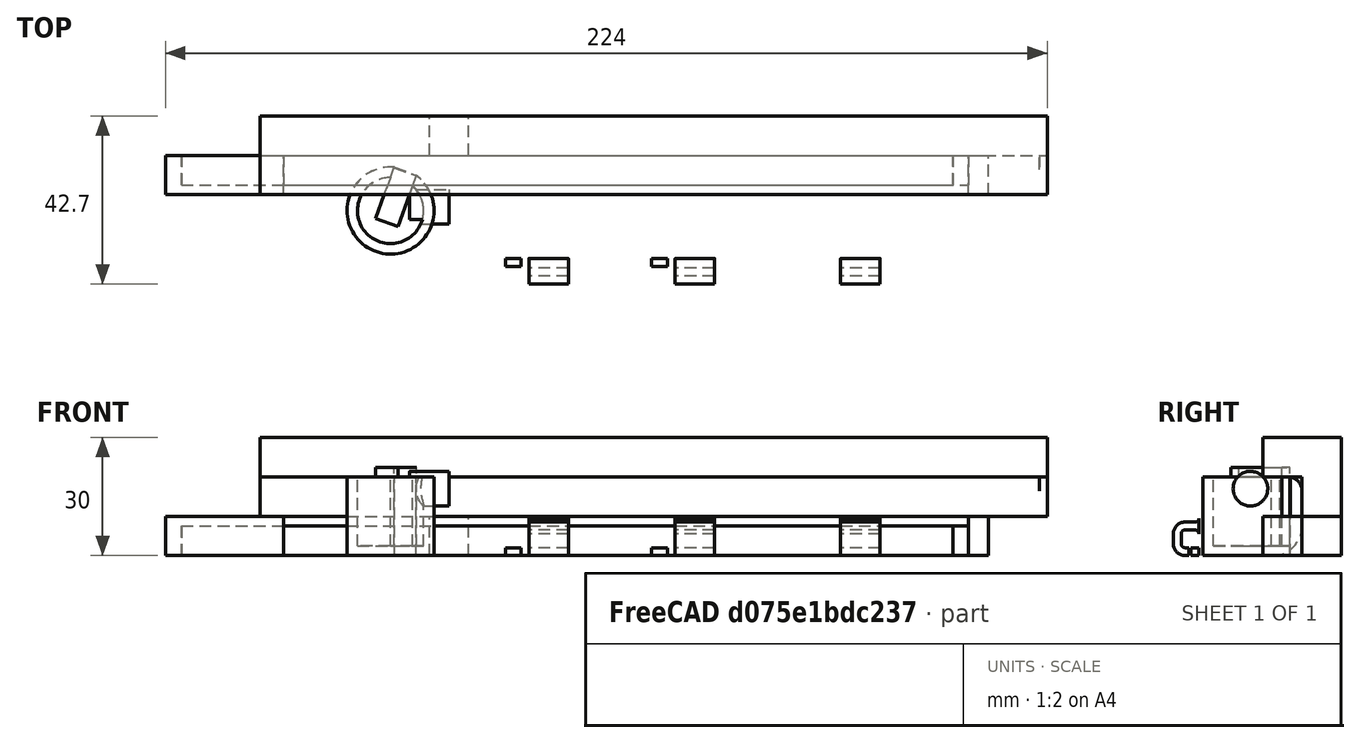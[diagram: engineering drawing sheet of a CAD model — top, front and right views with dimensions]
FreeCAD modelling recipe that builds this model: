
FCSTD DOCUMENT  (FreeCAD 0.19R0.19.2)
Label: v0_74
License: All rights reserved
LicenseURL: http://en.wikipedia.org/wiki/All_rights_reserved
objects: Part::Box×35, Part::Fillet×31, Part::MultiFuse×14, Part::Cut×13, Sketcher::SketchObject×11, Part::Extrusion×9, Part::Cylinder×6, App::MeasureDistance×5, Part::Revolution×1
note: 120 computed .brp shape members not serialized (recipe doc carries the construction recipe); baked Part::Feature solids carry a one-line shape summary decoded from their .brp

FEATURE [Sketcher::SketchObject] Sketch001
  FullyConstrained = true
  sketch-geometry (47):
    g0: Circle CenterX=-129.5 CenterY=-8 CenterZ=0 NormalX=0 NormalY=0 NormalZ=1 AngleXU=0 Radius=1
    g1: Circle CenterX=-129.5 CenterY=-3 CenterZ=0 NormalX=0 NormalY=0 NormalZ=1 AngleXU=0 Radius=1
    g2: Circle CenterX=-124.5 CenterY=-3 CenterZ=0 NormalX=0 NormalY=0 NormalZ=1 AngleXU=0 Radius=1
    g3: BSplineCurve PolesCount=3 KnotsCount=2 Degree=2 IsPeriodic=0
    g4: GeomPoint X=-129.5 Y=-8 Z=0
    g5: GeomPoint X=-124.5 Y=-3 Z=0
    g6: LineSegment StartX=18.6 StartY=-2.9 StartZ=0 EndX=23.6 EndY=-2.9 EndZ=0
    g7: ArcOfCircle CenterX=23.8 CenterY=-14.35 CenterZ=0 NormalX=0 NormalY=0 NormalZ=1 AngleXU=0 Radius=2.3 StartAngle=8e-16 EndAngle=1.5708
    g8: ArcOfCircle CenterX=23.8 CenterY=-18.1 CenterZ=0 NormalX=0 NormalY=0 NormalZ=1 AngleXU=0 Radius=2.3 StartAngle=4.71239 EndAngle=6.28319
    g9: LineSegment StartX=23.8 StartY=-20.4 StartZ=0 EndX=21.1 EndY=-20.4 EndZ=0
    g10: LineSegment StartX=21.1 StartY=-22.9 StartZ=0 EndX=21.1 EndY=-20.4 EndZ=0
    g11: LineSegment StartX=26.1 StartY=-14.35 StartZ=0 EndX=26.1 EndY=-18.1 EndZ=0
    g12: LineSegment StartX=18.6 StartY=-5.40742 StartZ=0 EndX=18.6 EndY=-2.9 EndZ=0
    g13: ArcOfCircle CenterX=18.8 CenterY=-8.1 CenterZ=0 NormalX=0 NormalY=0 NormalZ=1 AngleXU=0 Radius=2.7 StartAngle=1.64494 EndAngle=3.14159
    g14: ArcOfCircle CenterX=18.8 CenterY=-11.85 CenterZ=0 NormalX=0 NormalY=0 NormalZ=1 AngleXU=0 Radius=2.7 StartAngle=3.14159 EndAngle=4.71239
    g15: LineSegment StartX=16.1 StartY=-8.1 StartZ=0 EndX=16.1 EndY=-11.85 EndZ=0
    g16: LineSegment StartX=18.8 StartY=-14.55 StartZ=0 EndX=21.5 EndY=-14.55 EndZ=0
    g17: LineSegment StartX=21.5 StartY=-12.05 StartZ=0 EndX=21.5 EndY=-14.55 EndZ=0
    g18: LineSegment StartX=21.5 StartY=-12.05 StartZ=0 EndX=23.8 EndY=-12.05 EndZ=0
    g19: LineSegment StartX=16.1 StartY=-22.9 StartZ=0 EndX=21.1 EndY=-22.9 EndZ=0
    g20: LineSegment StartX=23.6 StartY=-2.9 StartZ=0 EndX=23.6 EndY=0 EndZ=0
    g21: LineSegment StartX=16.1 StartY=-22.9 StartZ=0 EndX=16.1 EndY=-26.2 EndZ=0
    g22: BSplineCurve PolesCount=3 KnotsCount=2 Degree=2 IsPeriodic=0
    g23: LineSegment StartX=2.6 StartY=-3 StartZ=0 EndX=-124.5 EndY=-3 EndZ=0
    g24: ArcOfCircle CenterX=-134.9 CenterY=-8.6 CenterZ=0 NormalX=0 NormalY=0 NormalZ=1 AngleXU=0 Radius=0.5 StartAngle=4.71238 EndAngle=6.28319
    g25: LineSegment StartX=-141.9 StartY=-9.1 StartZ=0 EndX=-134.9 EndY=-9.1 EndZ=0
    g26: LineSegment StartX=-141.9 StartY=-33.8 StartZ=0 EndX=-141.5 EndY=-33.8 EndZ=0
    g27: LineSegment StartX=-141.9 StartY=-9.1 StartZ=0 EndX=-141.9 EndY=-33.8 EndZ=0
    g28: LineSegment StartX=-134.4 StartY=-8.6 StartZ=0 EndX=-134.4 EndY=0 EndZ=0
    g29: LineSegment StartX=-134.4 StartY=0 StartZ=0 EndX=23.6 EndY=0 EndZ=0
    g30: LineSegment StartX=-133.5 StartY=-26.2 StartZ=0 EndX=16.1 EndY=-26.2 EndZ=0
    g31-g36: Circle x6 (B-spline internal-alignment scaffolding for g37; pole/knot coordinates omitted)
    g37: BSplineCurve PolesCount=6 KnotsCount=4 Degree=3 IsPeriodic=0
    g38-g41: GeomPoint x4 (B-spline internal-alignment scaffolding for g37; pole/knot coordinates omitted)
    g42: BSplineCurve PolesCount=3 KnotsCount=2 Degree=2 IsPeriodic=0
    g43: LineSegment StartX=-129.5 StartY=-8 StartZ=0 EndX=-129.5 EndY=-18.2 EndZ=0
    g44: BSplineCurve PolesCount=3 KnotsCount=2 Degree=2 IsPeriodic=0
    g45: LineSegment StartX=7.6 StartY=-8 StartZ=0 EndX=7.6 EndY=-18.2 EndZ=0
    g46: LineSegment StartX=2.6 StartY=-23.2 StartZ=0 EndX=-124.5 EndY=-23.2 EndZ=0
  constraints (87):
    c: Weight(g0) = 1
    c: Equal(g0,g1)
    c: Equal(g0,g2)
    c: InternalAlignment(g0,g3)
    c: InternalAlignment(g1,g3)
    c: InternalAlignment(g2,g3)
    c: InternalAlignment(g4,g3)
    c: InternalAlignment(g5,g3)
    c: Block(g3)
    c: Block(g8)
    c: Block(g7)
    c: Coincident(g9,g8)
    c: Horizontal(g9)
    c: Vertical(g10)
    c: Coincident(g10,g9)
    c: Coincident(g11,g7)
    c: Coincident(g11,g8)
    c: Vertical(g11)
    c: Vertical(g12)
    c: Block(g12)
    c: Coincident(g6,g12)
    c: Horizontal(g6)
    c: Block(g6)
    c: Coincident(g13,g12)
    c: Block(g14)
    c: Vertical(g15)
    c: Block(g15)
    c: Coincident(g16,g14)
    c: Horizontal(g16)
    c: Vertical(g17)
    c: Coincident(g17,g16)
    c: Block(g17)
    c: Coincident(g18,g7)
    c: Horizontal(g18)
    c: Block(g18)
    c: Coincident(g19,g10)
    c: Horizontal(g19)
    c: Block(g19)
    c: Block(g13)
    c: Coincident(g20,g6)
    c: Vertical(g20)
    c: Vertical(g21)
    c: Block(g21)
    c: Block(g22)
    c: Coincident(g23,g22)
    c: Coincident(g23,g3)
    c: Horizontal(g23)
    c: Block(g24)
    c: Coincident(g25,g24)
    c: Horizontal(g25)
    c: Horizontal(g26)
    c: Block(g26)
    c: Coincident(g27,g25)
    c: Coincident(g27,g26)
    c: Vertical(g27)
    c: Coincident(g28,g24)
    c: Vertical(g28)
    c: Coincident(g29,g28)
    c: Coincident(g29,g20)
    c: Horizontal(g29)
    c: Block(g29)
    c: Block(g25)
    c: Block(g28)
    c: Block(g27)
    c: Coincident(g30,g21)
    c: Horizontal(g30)
    c: Block(g30)
    c: Coincident(g37,g26)
    c: Weight(g31) = 1
    c: Equal(g31, g32-g36) x5
    c: Coincident(g37,g30)
    c: InternalAlignment(g31-g36 -> g37) x6
    c: InternalAlignment(g38-g41 -> g37) x4
    c: Block(g37)
    c: Block(g42)
    c: Coincident(g43,g3)
    c: Coincident(g43,g42)
    c: Vertical(g43)
    c: Distance(g43) = 10.2
    c: Block(g44)
    c: Coincident(g45,g22)
    c: Coincident(g45,g44)
    c: Vertical(g45)
    c: Distance(g45) = 10.2
    c: Coincident(g46,g44)
    c: Coincident(g46,g42)
    c: Horizontal(g46)
FEATURE [Part::Extrusion] Extrude001
  Base = -> Sketch001
  Dir = (0,0,1)
  DirMode = 2
  FaceMakerClass = Part::FaceMakerBullseye
  LengthFwd = 20
  LengthRev = 0
  Solid = true
  Symmetric = false
FEATURE [Sketcher::SketchObject] Sketch004
  FullyConstrained = true
  Placement = pos=(0,0,0) rot=(1,0,0;1.5708rad)
  sketch-geometry (12):
    g0: LineSegment StartX=15.75 StartY=2.5 StartZ=0 EndX=15.75 EndY=0 EndZ=0
    g1: Circle CenterX=15.75 CenterY=2.5 CenterZ=0 NormalX=0 NormalY=0 NormalZ=1 AngleXU=0 Radius=1
    g2: Circle CenterX=10.55 CenterY=2.5 CenterZ=0 NormalX=0 NormalY=0 NormalZ=1 AngleXU=0 Radius=1
    g3: Circle CenterX=10.55 CenterY=8 CenterZ=0 NormalX=0 NormalY=0 NormalZ=1 AngleXU=0 Radius=1
    g4: BSplineCurve PolesCount=3 KnotsCount=2 Degree=2 IsPeriodic=0
    g5: GeomPoint X=15.75 Y=2.5 Z=0
    g6: GeomPoint X=10.55 Y=8 Z=0
    g7: LineSegment StartX=1.9 StartY=8 StartZ=0 EndX=10.55 EndY=8 EndZ=0
    g8: LineSegment StartX=1.9 StartY=-2.4 StartZ=0 EndX=1.9 EndY=8 EndZ=0
    g9: LineSegment StartX=3.30092 StartY=-2.4 StartZ=0 EndX=3.30092 EndY=0 EndZ=0
    g10: LineSegment StartX=15.75 StartY=0 StartZ=0 EndX=3.30092 EndY=0 EndZ=0
    g11: LineSegment StartX=3.30092 StartY=-2.4 StartZ=0 EndX=1.9 EndY=-2.4 EndZ=0
  constraints (26):
    c: Vertical(g0)
    c: Distance(g0) = 2.5
    c: Coincident(g4,g0)
    c: Weight(g1) = 1
    c: Equal(g1,g2)
    c: Equal(g1,g3)
    c: InternalAlignment(g1,g4)
    c: InternalAlignment(g2,g4)
    c: InternalAlignment(g3,g4)
    c: InternalAlignment(g5,g4)
    c: InternalAlignment(g6,g4)
    c: Block(g4)
    c: Coincident(g7,g4)
    c: Horizontal(g7)
    c: Vertical(g8)
    c: Coincident(g8,g7)
    c: Block(g8)
    c: Vertical(g9)
    c: Coincident(g10,g0)
    c: PointOnObject(g10,g-1)
    c: Horizontal(g10)
    c: Coincident(g10,g9)
    c: Block(g9)
    c: Coincident(g11,g9)
    c: Coincident(g11,g8)
    c: Horizontal(g11)
FEATURE [Part::Revolution] Revolve  label="mainScrewStandRevolve"
  Angle = 360
  Axis = (0,0,1)
  Base = (0,0,0)
  FaceMakerClass = Part::FaceMakerBullseye
  Placement = pos=(-101.95,-15.3,0) rot=(0,0,1;0rad)
  Solid = true
  Source = -> Sketch004
  Symmetric = false
FEATURE [Sketcher::SketchObject] Sketch044
  FullyConstrained = true
  MapMode = 4
  Placement = pos=(0,0,0) rot=(0.57735,0.57735,0.57735;2.0944rad)
  sketch-geometry (14):
    g0: LineSegment StartX=6.08745 StartY=-4.11588 StartZ=0 EndX=6.08745 EndY=-2.11589 EndZ=0
    g1: LineSegment StartX=8.08745 StartY=1.38411 StartZ=0 EndX=8.08745 EndY=-1.11589 EndZ=0
    g2: ArcOfCircle CenterX=7.08745 CenterY=-1.11589 CenterZ=0 NormalX=0 NormalY=0 NormalZ=1 AngleXU=0 Radius=1 StartAngle=4.71239 EndAngle=6.28319
    g3: LineSegment StartX=6.08745 StartY=-2.11589 StartZ=0 EndX=7.08745 EndY=-2.11589 EndZ=0
    g4: LineSegment StartX=6.08745 StartY=-4.11588 StartZ=0 EndX=7.08745 EndY=-4.11588 EndZ=0
    g5: ArcOfCircle CenterX=7.08745 CenterY=-1.11589 CenterZ=0 NormalX=0 NormalY=0 NormalZ=1 AngleXU=0 Radius=3 StartAngle=4.71239 EndAngle=6.28319
    g6: ArcOfCircle CenterX=7.08745 CenterY=1.38411 CenterZ=0 NormalX=0 NormalY=0 NormalZ=1 AngleXU=0 Radius=1 StartAngle=5.35e-14 EndAngle=1.5708
    g7: LineSegment StartX=10.0875 StartY=-1.11588 StartZ=0 EndX=10.0875 EndY=1.38411 EndZ=0
    g8: ArcOfCircle CenterX=7.08745 CenterY=1.38411 CenterZ=0 NormalX=0 NormalY=0 NormalZ=1 AngleXU=0 Radius=3 StartAngle=3.57e-14 EndAngle=1.5708
    g9: ArcOfCircle CenterX=4.58745 CenterY=1.38412 CenterZ=0 NormalX=0 NormalY=0 NormalZ=1 AngleXU=0 Radius=1 StartAngle=1.57081 EndAngle=3.14159
    g10: LineSegment StartX=4.58744 StartY=2.38411 StartZ=0 EndX=7.08745 EndY=2.38411 EndZ=0
    g11: LineSegment StartX=4.58745 StartY=4.38411 StartZ=0 EndX=7.08745 EndY=4.38411 EndZ=0
    g12: ArcOfCircle CenterX=4.58745 CenterY=5.38411 CenterZ=0 NormalX=0 NormalY=0 NormalZ=1 AngleXU=0 Radius=1 StartAngle=3.14159 EndAngle=4.71239
    g13: LineSegment StartX=3.58745 StartY=5.38411 StartZ=0 EndX=3.58745 EndY=1.38411 EndZ=0
  constraints (33):
    c: Vertical(g0)
    c: Block(g0)
    c: Block(g1)
    c: Coincident(g2,g1)
    c: Coincident(g3,g0)
    c: Coincident(g3,g2)
    c: Horizontal(g3)
    c: Block(g2)
    c: Coincident(g4,g0)
    c: Horizontal(g4)
    c: Coincident(g5,g2)
    c: Block(g5)
    c: Block(g4)
    c: Coincident(g6,g1)
    c: Block(g6)
    c: Coincident(g7,g5)
    c: Vertical(g7)
    c: Coincident(g8,g6)
    c: Block(g8)
    c: Block(g7)
    c: Coincident(g10,g9)
    c: Coincident(g10,g6)
    c: Horizontal(g10)
    c: Block(g10)
    c: Block(g9)
    c: Coincident(g11,g8)
    c: Horizontal(g11)
    c: Block(g12)
    c: Block(g11)
    c: Coincident(g13,g12)
    c: Coincident(g13,g9)
    c: Vertical(g13)
    c: Tangent(g13,g9)
FEATURE [Sketcher::SketchObject] Sketch045
  FullyConstrained = true
  MapMode = 4
  Placement = pos=(0,0,0) rot=(0.57735,0.57735,0.57735;2.0944rad)
  sketch-geometry (14):
    g0: LineSegment StartX=6.08745 StartY=-4.11588 StartZ=0 EndX=6.08745 EndY=-2.11589 EndZ=0
    g1: LineSegment StartX=8.08745 StartY=1.38411 StartZ=0 EndX=8.08745 EndY=-1.11589 EndZ=0
    g2: ArcOfCircle CenterX=7.08745 CenterY=-1.11589 CenterZ=0 NormalX=0 NormalY=0 NormalZ=1 AngleXU=0 Radius=1 StartAngle=4.71239 EndAngle=6.28319
    g3: LineSegment StartX=6.08745 StartY=-2.11589 StartZ=0 EndX=7.08745 EndY=-2.11589 EndZ=0
    g4: LineSegment StartX=6.08745 StartY=-4.11588 StartZ=0 EndX=7.08745 EndY=-4.11588 EndZ=0
    g5: ArcOfCircle CenterX=7.08745 CenterY=-1.11589 CenterZ=0 NormalX=0 NormalY=0 NormalZ=1 AngleXU=0 Radius=3 StartAngle=4.71239 EndAngle=6.28319
    g6: ArcOfCircle CenterX=7.08745 CenterY=1.38411 CenterZ=0 NormalX=0 NormalY=0 NormalZ=1 AngleXU=0 Radius=1 StartAngle=5.35e-14 EndAngle=1.5708
    g7: LineSegment StartX=10.0875 StartY=-1.11588 StartZ=0 EndX=10.0875 EndY=1.38411 EndZ=0
    g8: ArcOfCircle CenterX=7.08745 CenterY=1.38411 CenterZ=0 NormalX=0 NormalY=0 NormalZ=1 AngleXU=0 Radius=3 StartAngle=3.57e-14 EndAngle=1.5708
    g9: ArcOfCircle CenterX=4.58745 CenterY=1.38412 CenterZ=0 NormalX=0 NormalY=0 NormalZ=1 AngleXU=0 Radius=1 StartAngle=1.57081 EndAngle=3.14159
    g10: LineSegment StartX=4.58744 StartY=2.38411 StartZ=0 EndX=7.08745 EndY=2.38411 EndZ=0
    g11: LineSegment StartX=4.58745 StartY=4.38411 StartZ=0 EndX=7.08745 EndY=4.38411 EndZ=0
    g12: ArcOfCircle CenterX=4.58745 CenterY=5.38411 CenterZ=0 NormalX=0 NormalY=0 NormalZ=1 AngleXU=0 Radius=1 StartAngle=3.14159 EndAngle=4.71239
    g13: LineSegment StartX=3.58745 StartY=5.38411 StartZ=0 EndX=3.58745 EndY=1.38411 EndZ=0
  constraints (33):
    c: Vertical(g0)
    c: Block(g0)
    c: Block(g1)
    c: Coincident(g2,g1)
    c: Coincident(g3,g0)
    c: Coincident(g3,g2)
    c: Horizontal(g3)
    c: Block(g2)
    c: Coincident(g4,g0)
    c: Horizontal(g4)
    c: Coincident(g5,g2)
    c: Block(g5)
    c: Block(g4)
    c: Coincident(g6,g1)
    c: Block(g6)
    c: Coincident(g7,g5)
    c: Vertical(g7)
    c: Coincident(g8,g6)
    c: Block(g8)
    c: Block(g7)
    c: Coincident(g10,g9)
    c: Coincident(g10,g6)
    c: Horizontal(g10)
    c: Block(g10)
    c: Block(g9)
    c: Coincident(g11,g8)
    c: Horizontal(g11)
    c: Block(g12)
    c: Block(g11)
    c: Coincident(g13,g12)
    c: Coincident(g13,g9)
    c: Vertical(g13)
    c: Tangent(g13,g9)
FEATURE [Part::Extrusion] Extrude040
  Base = -> Sketch045
  Dir = (1,0,0)
  DirMode = 2
  FaceMakerClass = Part::FaceMakerBullseye
  LengthFwd = 10
  LengthRev = 0
  Placement = pos=(-71.7,-22.61,4.115) rot=(0,0,1;3.14159rad)
  Solid = true
  Symmetric = false
FEATURE [Part::Box] Box017  label="Cube017"
  AttacherType = Attacher::AttachEngine3D
  Height = 2
  Length = 2
  Placement = pos=(-85.7,-21.3,0) rot=(0,0,1;0rad)
  Width = 2
FEATURE [Part::Box] Box018  label="Cube018"
  AttacherType = Attacher::AttachEngine3D
  Height = 2
  Length = 2
  Placement = pos=(-87.7,-21.3,0) rot=(0,0,1;0rad)
  Width = 2
FEATURE [Part::MultiFuse] Fusion
  Placement = pos=(0,-6.9,0) rot=(0,0,1;0rad)
  Shapes = -> [Box017,Box018]
FEATURE [Part::Box] Box  label="Cube"
  AttacherType = Attacher::AttachEngine3D
  Height = 10
  Length = 10
  Placement = pos=(-107,0,0) rot=(0,0,1;0rad)
  Width = 10
FEATURE [Sketcher::SketchObject] Sketch046
  FullyConstrained = true
  MapMode = 4
  Placement = pos=(0,0,0) rot=(0.57735,0.57735,0.57735;2.0944rad)
  sketch-geometry (14):
    g0: LineSegment StartX=6.08745 StartY=-4.11588 StartZ=0 EndX=6.08745 EndY=-2.11589 EndZ=0
    g1: LineSegment StartX=8.08745 StartY=1.38411 StartZ=0 EndX=8.08745 EndY=-1.11589 EndZ=0
    g2: ArcOfCircle CenterX=7.08745 CenterY=-1.11589 CenterZ=0 NormalX=0 NormalY=0 NormalZ=1 AngleXU=0 Radius=1 StartAngle=4.71239 EndAngle=6.28319
    g3: LineSegment StartX=6.08745 StartY=-2.11589 StartZ=0 EndX=7.08745 EndY=-2.11589 EndZ=0
    g4: LineSegment StartX=6.08745 StartY=-4.11588 StartZ=0 EndX=7.08745 EndY=-4.11588 EndZ=0
    g5: ArcOfCircle CenterX=7.08745 CenterY=-1.11589 CenterZ=0 NormalX=0 NormalY=0 NormalZ=1 AngleXU=0 Radius=3 StartAngle=4.71239 EndAngle=6.28319
    g6: ArcOfCircle CenterX=7.08745 CenterY=1.38411 CenterZ=0 NormalX=0 NormalY=0 NormalZ=1 AngleXU=0 Radius=1 StartAngle=5.35e-14 EndAngle=1.5708
    g7: LineSegment StartX=10.0875 StartY=-1.11588 StartZ=0 EndX=10.0875 EndY=1.38411 EndZ=0
    g8: ArcOfCircle CenterX=7.08745 CenterY=1.38411 CenterZ=0 NormalX=0 NormalY=0 NormalZ=1 AngleXU=0 Radius=3 StartAngle=3.57e-14 EndAngle=1.5708
    g9: ArcOfCircle CenterX=4.58745 CenterY=1.38412 CenterZ=0 NormalX=0 NormalY=0 NormalZ=1 AngleXU=0 Radius=1 StartAngle=1.57081 EndAngle=3.14159
    g10: LineSegment StartX=4.58744 StartY=2.38411 StartZ=0 EndX=7.08745 EndY=2.38411 EndZ=0
    g11: LineSegment StartX=4.58745 StartY=4.38411 StartZ=0 EndX=7.08745 EndY=4.38411 EndZ=0
    g12: ArcOfCircle CenterX=4.58745 CenterY=5.38411 CenterZ=0 NormalX=0 NormalY=0 NormalZ=1 AngleXU=0 Radius=1 StartAngle=3.14159 EndAngle=4.71239
    g13: LineSegment StartX=3.58745 StartY=5.38411 StartZ=0 EndX=3.58745 EndY=1.38411 EndZ=0
  constraints (33):
    c: Vertical(g0)
    c: Block(g0)
    c: Block(g1)
    c: Coincident(g2,g1)
    c: Coincident(g3,g0)
    c: Coincident(g3,g2)
    c: Horizontal(g3)
    c: Block(g2)
    c: Coincident(g4,g0)
    c: Horizontal(g4)
    c: Coincident(g5,g2)
    c: Block(g5)
    c: Block(g4)
    c: Coincident(g6,g1)
    c: Block(g6)
    c: Coincident(g7,g5)
    c: Vertical(g7)
    c: Coincident(g8,g6)
    c: Block(g8)
    c: Block(g7)
    c: Coincident(g10,g9)
    c: Coincident(g10,g6)
    c: Horizontal(g10)
    c: Block(g10)
    c: Block(g9)
    c: Coincident(g11,g8)
    c: Horizontal(g11)
    c: Block(g12)
    c: Block(g11)
    c: Coincident(g13,g12)
    c: Coincident(g13,g9)
    c: Vertical(g13)
    c: Tangent(g13,g9)
FEATURE [Part::Extrusion] Extrude041
  Base = -> Sketch046
  Dir = (1,0,0)
  DirMode = 2
  FaceMakerClass = Part::FaceMakerBullseye
  LengthFwd = 10
  LengthRev = 0
  Placement = pos=(7.5,-22.61,4.115) rot=(0,0,1;3.14159rad)
  Solid = true
  Symmetric = false
FEATURE [Part::Box] Box042  label="Cube042"
  AttacherType = Attacher::AttachEngine3D
  Height = 2
  Length = 2
  Placement = pos=(-87.7,-21.3,0) rot=(0,0,1;0rad)
  Width = 2
FEATURE [Part::Box] Box043  label="Cube043"
  AttacherType = Attacher::AttachEngine3D
  Height = 2
  Length = 2
  Placement = pos=(-85.7,-21.3,0) rot=(0,0,1;0rad)
  Width = 2
FEATURE [Part::MultiFuse] Fusion019
  Placement = pos=(37.15,-6.9,0) rot=(0,0,1;0rad)
  Shapes = -> [Box043,Box042]
FEATURE [Part::Box] Box005  label="Cube005"
  AttacherType = Attacher::AttachEngine3D
  Height = 10
  Length = 198
  Placement = pos=(-30,0,0) rot=(0,0,1;0rad)
  Width = 10
FEATURE [Part::Box] Box004  label="Cube004"
  AttacherType = Attacher::AttachEngine3D
  Height = 10
  Length = 200
  Placement = pos=(-30,0,0) rot=(0,0,1;0rad)
  Width = 10
FEATURE [Part::Fillet] Fillet020
  Base = -> Box004
  Edges = 1 edges r=3.6: [Edge12]
FEATURE [Sketcher::SketchObject] Sketch
  FullyConstrained = true
  sketch-geometry (35):
    g0: Circle CenterX=-101.95 CenterY=-14.3 CenterZ=0 NormalX=0 NormalY=0 NormalZ=1 AngleXU=0 Radius=3.25
    g1: LineSegment StartX=16.1 StartY=-26.2 StartZ=0 EndX=16.1 EndY=-22.9 EndZ=0
    g2: ArcOfCircle CenterX=23.8 CenterY=-14.35 CenterZ=0 NormalX=0 NormalY=0 NormalZ=1 AngleXU=0 Radius=2.3 StartAngle=8e-16 EndAngle=1.5708
    g3: LineSegment StartX=18.6 StartY=-5.40742 StartZ=0 EndX=18.6 EndY=-2.9 EndZ=0
    g4: LineSegment StartX=18.6 StartY=-2.9 StartZ=0 EndX=23.6 EndY=-2.9 EndZ=0
    g5: LineSegment StartX=23.6 StartY=-2.9 StartZ=0 EndX=23.6 EndY=2.58e-14 EndZ=0
    g6: LineSegment StartX=18.8 StartY=-14.55 StartZ=0 EndX=21.5 EndY=-14.55 EndZ=0
    g7: LineSegment StartX=21.5 StartY=-12.05 StartZ=0 EndX=21.5 EndY=-14.55 EndZ=0
    g8: LineSegment StartX=21.5 StartY=-12.05 StartZ=0 EndX=23.8 EndY=-12.05 EndZ=0
    g9: ArcOfCircle CenterX=23.8 CenterY=-18.1 CenterZ=0 NormalX=0 NormalY=0 NormalZ=1 AngleXU=0 Radius=2.3 StartAngle=4.71239 EndAngle=6.28319
    g10: LineSegment StartX=23.8 StartY=-20.4 StartZ=0 EndX=21.1 EndY=-20.4 EndZ=0
    g11: LineSegment StartX=26.1 StartY=-14.35 StartZ=0 EndX=26.1 EndY=-18.1 EndZ=0
    g12: ArcOfCircle CenterX=18.8 CenterY=-8.1 CenterZ=0 NormalX=0 NormalY=0 NormalZ=1 AngleXU=0 Radius=2.7 StartAngle=1.64494 EndAngle=3.14159
    g13: ArcOfCircle CenterX=18.8 CenterY=-11.85 CenterZ=0 NormalX=0 NormalY=0 NormalZ=1 AngleXU=0 Radius=2.7 StartAngle=3.14159 EndAngle=4.71239
    g14: LineSegment StartX=16.1 StartY=-8.1 StartZ=0 EndX=16.1 EndY=-11.85 EndZ=0
    g15: LineSegment StartX=21.1 StartY=-22.9 StartZ=0 EndX=21.1 EndY=-20.4 EndZ=0
    g16: LineSegment StartX=16.1 StartY=-22.9 StartZ=0 EndX=21.1 EndY=-22.9 EndZ=0
    g17: LineSegment StartX=23.6 StartY=2.58e-14 StartZ=0 EndX=-134.4 EndY=2.58e-14 EndZ=0
    g18: LineSegment StartX=-134.4 StartY=2.59e-14 StartZ=0 EndX=-134.4 EndY=-8.6 EndZ=0
    g19: ArcOfCircle CenterX=-134.9 CenterY=-8.6 CenterZ=0 NormalX=0 NormalY=0 NormalZ=1 AngleXU=0 Radius=0.5 StartAngle=4.71238 EndAngle=6.28319
    g20: LineSegment StartX=-134.9 StartY=-9.1 StartZ=0 EndX=-141.9 EndY=-9.1 EndZ=0
    g21: LineSegment StartX=-141.9 StartY=-9.1 StartZ=0 EndX=-141.9 EndY=-33.8 EndZ=0
    g22: LineSegment StartX=-141.9 StartY=-33.8 StartZ=0 EndX=-141.5 EndY=-33.8 EndZ=0
    g23: LineSegment StartX=-133.5 StartY=-26.2 StartZ=0 EndX=16.1 EndY=-26.2 EndZ=0
    g24-g29: Circle x6 (B-spline internal-alignment scaffolding for g30; pole/knot coordinates omitted)
    g30: BSplineCurve PolesCount=6 KnotsCount=4 Degree=3 IsPeriodic=0
    g31-g34: GeomPoint x4 (B-spline internal-alignment scaffolding for g30; pole/knot coordinates omitted)
  constraints (61):
    c: Block(g0)
    c: Vertical(g1)
    c: Distance(g1) = 3.3
    c: Block(g9)
    c: Block(g2)
    c: Coincident(g10,g9)
    c: Horizontal(g10)
    c: Vertical(g15)
    c: Coincident(g15,g10)
    c: Coincident(g11,g2)
    c: Coincident(g11,g9)
    c: Vertical(g11)
    c: Vertical(g3)
    c: Block(g3)
    c: Coincident(g4,g3)
    c: Horizontal(g4)
    c: Vertical(g5)
    c: Block(g5)
    c: Block(g4)
    c: Coincident(g12,g3)
    c: Block(g13)
    c: Coincident(g14,g12)
    c: Vertical(g14)
    c: Block(g14)
    c: Coincident(g6,g13)
    c: Horizontal(g6)
    c: Vertical(g7)
    c: Coincident(g7,g6)
    c: Block(g7)
    c: Coincident(g8,g2)
    c: Horizontal(g8)
    c: Block(g8)
    c: Coincident(g16,g15)
    c: Horizontal(g16)
    c: Block(g16)
    c: Block(g12)
    c: Coincident(g16,g1)
    c: Coincident(g17,g5)
    c: Horizontal(g17)
    c: Vertical(g18)
    c: Horizontal(g20)
    c: Coincident(g19,g18)
    c: Coincident(g19,g20)
    c: Block(g19)
    c: Coincident(g21,g20)
    c: Vertical(g21)
    c: Block(g21)
    c: Coincident(g22,g21)
    c: Horizontal(g22)
    c: Block(g22)
    c: Block(g18)
    c: Coincident(g18,g17)
    c: Coincident(g23,g1)
    c: Horizontal(g23)
    c: Distance(g23) = 149.6
    c: Coincident(g30,g22)
    c: Weight(g24) = 1
    c: Equal(g24, g25-g29) x5
    c: InternalAlignment(g24-g29 -> g30) x6
    c: InternalAlignment(g31-g34 -> g30) x4
    c: Block(g30)
FEATURE [Part::Extrusion] Extrude
  Base = -> Sketch
  Dir = (0,0,1)
  DirMode = 2
  FaceMakerClass = Part::FaceMakerBullseye
  LengthFwd = 2.4
  LengthRev = 0
  Solid = true
  Symmetric = false
FEATURE [Part::Box] Box051  label="Cube051"
  AttacherType = Attacher::AttachEngine3D
  Height = 10
  Length = 198
  Placement = pos=(-30,0,0) rot=(0,0,1;0rad)
  Width = 10
FEATURE [Part::Box] Box052  label="Cube052"
  AttacherType = Attacher::AttachEngine3D
  Height = 5
  Length = 200
  Placement = pos=(-30,6.4,10) rot=(1,0,0;0rad)
  Width = 5
FEATURE [Part::Box] Box053  label="Cube053"
  AttacherType = Attacher::AttachEngine3D
  Height = 5
  Length = 200
  Placement = pos=(-30,6.4,10) rot=(1,0,0;0.872665rad)
  Width = 5
FEATURE [Part::Box] Box054  label="Cube054"
  AttacherType = Attacher::AttachEngine3D
  Height = 10
  Length = 200
  Placement = pos=(-30,0,0) rot=(0,0,1;0rad)
  Width = 10
FEATURE [Part::Fillet] Fillet021
  Base = -> Box054
  Edges = 1 edges r=3.6: [Edge12]
FEATURE [Part::Cut] Cut015
  Base = -> Box051
  Tool = -> Fillet021
FEATURE [Part::MultiFuse] Fusion033  label="removeFromMainFusion014"
  Placement = pos=(-120,-10,10) rot=(0,0,1;0rad)
  Shapes = -> [Box053,Box052,Cut015]
FEATURE [Part::Box] Box055  label="Cube055"
  AttacherType = Attacher::AttachEngine3D
  Height = 10
  Length = 190
  Placement = pos=(-30,0,0) rot=(0,0,1;0rad)
  Width = 10
FEATURE [Part::Box] Box056  label="Cube056"
  AttacherType = Attacher::AttachEngine3D
  Height = 10
  Length = 190
  Placement = pos=(-35,0,0) rot=(0,0,1;0rad)
  Width = 10
FEATURE [Part::Fillet] Fillet022
  Base = -> Box055
  Edges = 1 edges r=7.5: [Edge11]
FEATURE [Part::Cut] Cut014  label="filletMain001"
  Base = -> Box056
  Placement = pos=(-120,-10,0) rot=(0,0,1;0rad)
  Tool = -> Fillet022
FEATURE [Part::MultiFuse] Fusion032  label="removeFromMain001"
  Shapes = -> [Fusion033,Cut014]
FEATURE [Part::Cut] Cut017
  Base = -> Extrude
  Tool = -> Fusion032
FEATURE [Part::Box] Box063  label="Cube063"
  AttacherType = Attacher::AttachEngine3D
  Height = 10
  Length = 198
  Placement = pos=(-30,0,0) rot=(0,0,1;0rad)
  Width = 10
FEATURE [Part::Box] Box064  label="Cube064"
  AttacherType = Attacher::AttachEngine3D
  Height = 5
  Length = 200
  Placement = pos=(-30,6.4,10) rot=(1,0,0;0rad)
  Width = 5
FEATURE [Part::Box] Box065  label="Cube065"
  AttacherType = Attacher::AttachEngine3D
  Height = 5
  Length = 200
  Placement = pos=(-30,6.4,10) rot=(1,0,0;0.872665rad)
  Width = 5
FEATURE [Part::Box] Box066  label="Cube066"
  AttacherType = Attacher::AttachEngine3D
  Height = 10
  Length = 200
  Placement = pos=(-30,0,0) rot=(0,0,1;0rad)
  Width = 10
FEATURE [Part::Fillet] Fillet023
  Base = -> Box066
  Edges = 1 edges r=3.6: [Edge12]
FEATURE [Part::Cut] Cut018
  Base = -> Box063
  Tool = -> Fillet023
FEATURE [Part::MultiFuse] Fusion035  label="removeFromMainFusion015"
  Placement = pos=(-120,-10,10) rot=(0,0,1;0rad)
  Shapes = -> [Box065,Box064,Cut018]
FEATURE [Part::Box] Box067  label="Cube067"
  AttacherType = Attacher::AttachEngine3D
  Height = 10
  Length = 190
  Placement = pos=(-30,0,0) rot=(0,0,1;0rad)
  Width = 10
FEATURE [Part::Fillet] Fillet024
  Base = -> Box067
  Edges = 1 edges r=7.5: [Edge11]
FEATURE [Part::Box] Box068  label="Cube068"
  AttacherType = Attacher::AttachEngine3D
  Height = 10
  Length = 190
  Placement = pos=(-35,0,0) rot=(0,0,1;0rad)
  Width = 10
FEATURE [Part::Cut] Cut019  label="filletMain002"
  Base = -> Box068
  Placement = pos=(-120,-10,0) rot=(0,0,1;0rad)
  Tool = -> Fillet024
FEATURE [Part::MultiFuse] Fusion036  label="removeFromMain002"
  Shapes = -> [Fusion035,Cut019]
FEATURE [Part::Box] Box069  label="Cube069"
  AttacherType = Attacher::AttachEngine3D
  Height = 20
  Length = 10
  Placement = pos=(-144.4,-8,0) rot=(0,0,1;0rad)
  Width = 10
FEATURE [Part::Box] Box070  label="Cube070"
  AttacherType = Attacher::AttachEngine3D
  Height = 20
  Length = 30
  Placement = pos=(-120,0,0) rot=(0,0,1;0rad)
  Width = 20
FEATURE [Part::MultiFuse] Fusion037  label="removeFromIntegrityIncreaserFusion037"
  Shapes = -> [Box069,Box070,Fusion036]
FEATURE [Sketcher::SketchObject] Sketch047
  FullyConstrained = true
  sketch-geometry (4):
    g0: LineSegment StartX=20.5 StartY=-1.82002 StartZ=0 EndX=20.5 EndY=-36 EndZ=0
    g1: LineSegment StartX=32.7 StartY=-36 StartZ=0 EndX=32.7 EndY=-1.82002 EndZ=0
    g2: LineSegment StartX=20.5 StartY=-1.82002 StartZ=0 EndX=32.7 EndY=-1.82002 EndZ=0
    g3: LineSegment StartX=20.5 StartY=-36 StartZ=0 EndX=32.7 EndY=-36 EndZ=0
  constraints (12):
    c: Vertical(g0)
    c: Distance(g0) = 34.18
    c: Vertical(g1)
    c: Block(g0)
    c: Coincident(g2,g0)
    c: Horizontal(g2)
    c: Coincident(g2,g1)
    c: Block(g2)
    c: Block(g1)
    c: Coincident(g3,g0)
    c: Coincident(g3,g1)
    c: Horizontal(g3)
FEATURE [Part::Cut] Cut021
  Base = -> Box005
  Tool = -> Fillet020
FEATURE [Part::Box] Box073  label="Cube073"
  AttacherType = Attacher::AttachEngine3D
  Height = 10
  Length = 200
  Placement = pos=(-30,10,0) rot=(0,0,1;0rad)
  Width = 10
FEATURE [Part::Box] Box074  label="Cube074"
  AttacherType = Attacher::AttachEngine3D
  Height = 10
  Length = 200
  Placement = pos=(-30,0,10) rot=(0,0,1;0rad)
  Width = 10
FEATURE [Part::Box] Box075  label="Cube075"
  AttacherType = Attacher::AttachEngine3D
  Height = 10
  Length = 200
  Placement = pos=(-30,10,10) rot=(0,0,1;0rad)
  Width = 10
FEATURE [Part::MultiFuse] Fusion043  label="removeFromMainFusion043"
  Placement = pos=(-120,-10,10) rot=(0,0,1;0rad)
  Shapes = -> [Cut021,Box074,Box073,Box075]
FEATURE [Part::Box] Box076  label="Cube076"
  AttacherType = Attacher::AttachEngine3D
  Height = 10
  Length = 200
  Placement = pos=(-160,0,0) rot=(0,0,1;0rad)
  Width = 10
FEATURE [Part::Box] Box077  label="Cube077"
  AttacherType = Attacher::AttachEngine3D
  Height = 10
  Length = 170
  Placement = pos=(-130,0,0) rot=(0,0,1;0rad)
  Width = 10
FEATURE [Part::Fillet] Fillet028
  Base = -> Box077
  Edges = 1 edges r=7.5: [Edge11]
FEATURE [Part::Cut] Cut024
  Base = -> Box076
  Placement = pos=(-14,-10,0) rot=(0,0,1;0rad)
  Tool = -> Fillet028
FEATURE [Part::Box] Box078  label="Cube078"
  AttacherType = Attacher::AttachEngine3D
  Height = 10
  Length = 200
  Width = 10
FEATURE [Part::Box] Box079  label="Cube079"
  AttacherType = Attacher::AttachEngine3D
  Height = 10
  Length = 205
  Placement = pos=(10,0,0) rot=(0,0,1;0rad)
  Width = 10
FEATURE [Part::Fillet] Fillet029
  Base = -> Box078
  Edges = 1 edges r=7.5: [Edge11]
  Placement = pos=(10,0,0) rot=(0,0,1;0rad)
FEATURE [Part::Cut] Cut025  label="removeFromMainCut025"
  Base = -> Box079
  Placement = pos=(-180,-10,0) rot=(0,0,1;0rad)
  Tool = -> Fillet029
FEATURE [Part::Cylinder] Cylinder001
  Angle = 360
  AttacherType = Attacher::AttachEngine3D
  Height = 10
  Placement = pos=(-36.2,-2,12) rot=(0,1,0;1.5708rad)
  Radius = 2
FEATURE [App::MeasureDistance] Distance  label="Distance: 4.02 mm"
  Distance = 4.02
  P1 = (-33.21,5.8978,9.90268)
  P2 = (-29.19,5.8978,9.90268)
FEATURE [Part::Fillet] Fillet030
  Base = -> Cylinder001
  Edges = 1 edges r=1.8: [Edge3]
FEATURE [Part::Fillet] Fillet031
  Base = -> Fillet030
  Edges = 1 edges r=1.8: [Edge2]
FEATURE [Part::Cylinder] Cylinder003
  Angle = 360
  AttacherType = Attacher::AttachEngine3D
  Height = 10
  Placement = pos=(-36.2,-2,12) rot=(0,1,0;1.5708rad)
  Radius = 2
FEATURE [Part::Fillet] Fillet035
  Base = -> Cylinder003
  Edges = 1 edges r=1.8: [Edge3]
FEATURE [Part::Fillet] Fillet036
  Base = -> Fillet035
  Edges = 1 edges r=1.8: [Edge2]
  Placement = pos=(-12.8,0,0) rot=(0,0,1;0rad)
FEATURE [Part::Cylinder] Cylinder004
  Angle = 360
  AttacherType = Attacher::AttachEngine3D
  Height = 10
  Placement = pos=(-36.2,-2,12) rot=(0,1,0;1.5708rad)
  Radius = 2
FEATURE [Part::Fillet] Fillet038
  Base = -> Cylinder004
  Edges = 1 edges r=1.8: [Edge3]
FEATURE [Part::Fillet] Fillet037
  Base = -> Fillet038
  Edges = 1 edges r=1.8: [Edge2]
  Placement = pos=(-6.4,0,0) rot=(0,0,1;0rad)
FEATURE [Sketcher::SketchObject] Sketch048
  FullyConstrained = true
  sketch-geometry (4):
    g0: LineSegment StartX=-5.1 StartY=-34.18 StartZ=0 EndX=5.1 EndY=-34.18 EndZ=0
    g1: LineSegment StartX=-5.1 StartY=-3.93167e-07 StartZ=0 EndX=-5.1 EndY=-34.18 EndZ=0
    g2: LineSegment StartX=5.1 StartY=-34.18 StartZ=0 EndX=5.1 EndY=-3.93167e-07 EndZ=0
    g3: LineSegment StartX=-5.1 StartY=-3.93167e-07 StartZ=0 EndX=5.1 EndY=-3.93167e-07 EndZ=0
  constraints (10):
    c: Horizontal(g0)
    c: Block(g0)
    c: Coincident(g1,g0)
    c: Vertical(g1)
    c: Coincident(g2,g0)
    c: Vertical(g2)
    c: Coincident(g3,g1)
    c: Coincident(g3,g2)
    c: Horizontal(g3)
    c: Block(g3)
FEATURE [Part::Extrusion] Extrude044
  Base = -> Sketch048
  Dir = (0,0,1)
  DirMode = 2
  FaceMakerClass = Part::FaceMakerBullseye
  LengthFwd = 6.2
  LengthRev = 0
  Solid = true
  Symmetric = false
FEATURE [Part::Fillet] Fillet039
  Base = -> Extrude044
  Edges = 1 edges r=3.09: [Edge7]
FEATURE [Part::Fillet] Fillet040
  Base = -> Fillet039
  Edges = 1 edges r=3.09: [Edge8]
FEATURE [Part::Fillet] Fillet041
  Base = -> Fillet040
  Edges = 1 edges r=3.09: [Edge17]
FEATURE [Part::Fillet] Fillet042  label="removeFromMainToMakeUSBCableHole"
  Base = -> Fillet041
  Edges = 1 edges r=3.09: [Edge10]
  Placement = pos=(-111.4,30,10.9) rot=(0,1,0;1.5708rad)
FEATURE [Part::Cylinder] Cylinder
  Angle = 360
  AttacherType = Attacher::AttachEngine3D
  Height = 17.6
  Placement = pos=(-116.86,-14.05,2.4) rot=(0,0,1;0rad)
  Radius = 8.4
FEATURE [Part::Box] Box080  label="Cube080"
  AttacherType = Attacher::AttachEngine3D
  Height = 20
  Length = 6
  Placement = pos=(-120.65,-16.05,2.4) rot=(0,0,-1;0.349066rad)
  Width = 13.85
FEATURE [Part::Cylinder] Cylinder005
  Angle = 360
  AttacherType = Attacher::AttachEngine3D
  Height = 20
  Placement = pos=(-116.86,-14.05,30) rot=(0,0,1;0rad)
  Radius = 11.06
FEATURE [Part::Box] Box081  label="Cube081"
  AttacherType = Attacher::AttachEngine3D
  Height = 20
  Length = 10
  Placement = pos=(-115.9,-3.3,30) rot=(0,0,-1;0.314159rad)
  Width = 10
FEATURE [App::MeasureDistance] Distance001  label="Distance: 2.40 mm"
  Distance = 2.4
  P1 = (-129.5,-19.3,2.4)
  P2 = (-129.5,-19.3,0)
FEATURE [Part::MultiFuse] Fusion047
  Shapes = -> [Box080,Cylinder]
FEATURE [Part::Cylinder] Cylinder006
  Angle = 360
  AttacherType = Attacher::AttachEngine3D
  Height = 10
  Placement = pos=(-112,-13.1,17) rot=(0,1,0;1.5708rad)
  Radius = 4.4
FEATURE [Part::MultiFuse] Fusion048  label="removeFromMainToCreateHoleForUSBCablePillar"
  Shapes = -> [Fusion047,Cylinder006]
FEATURE [Part::Extrusion] Extrude046
  Base = -> Sketch047
  Dir = (0,0,1)
  DirMode = 2
  FaceMakerClass = Part::FaceMakerBullseye
  LengthFwd = 8
  LengthRev = 0
  Solid = true
  Symmetric = false
FEATURE [App::MeasureDistance] Distance002  label="Distance: 12.20 mm"
  Distance = 12.2
  P1 = (32.7,-36,8)
  P2 = (20.5,-36,8)
FEATURE [Part::Fillet] Fillet
  Base = -> Extrude046
  Edges = 1 edges r=3.9: [Edge12]
FEATURE [Part::Fillet] Fillet048
  Base = -> Fillet
  Edges = 1 edges r=3.9: [Edge8]
FEATURE [Part::Fillet] Fillet049
  Base = -> Fillet048
  Edges = 1 edges r=3.9: [Edge17]
FEATURE [Part::Fillet] Fillet050
  Base = -> Fillet049
  Edges = 1 edges r=3.9: [Edge11]
  Placement = pos=(-55,0,8.3) rot=(1,0,0;0.191986rad)
FEATURE [Part::MultiFuse] Fusion049
  Shapes = -> [Fillet031,Fillet036,Fillet037]
FEATURE [Part::Cut] Cut027
  Base = -> Cylinder005
  Placement = pos=(0,0,-30) rot=(0,0,1;0rad)
  Tool = -> Box081
FEATURE [Sketcher::SketchObject] Sketch049
  FullyConstrained = true
  sketch-geometry (4):
    g0: LineSegment StartX=-5.1 StartY=-34.18 StartZ=0 EndX=5.1 EndY=-34.18 EndZ=0
    g1: LineSegment StartX=-5.1 StartY=-3.93167e-07 StartZ=0 EndX=-5.1 EndY=-34.18 EndZ=0
    g2: LineSegment StartX=5.1 StartY=-34.18 StartZ=0 EndX=5.1 EndY=-3.93167e-07 EndZ=0
    g3: LineSegment StartX=-5.1 StartY=-3.93167e-07 StartZ=0 EndX=5.1 EndY=-3.93167e-07 EndZ=0
  constraints (10):
    c: Horizontal(g0)
    c: Block(g0)
    c: Coincident(g1,g0)
    c: Vertical(g1)
    c: Coincident(g2,g0)
    c: Vertical(g2)
    c: Coincident(g3,g1)
    c: Coincident(g3,g2)
    c: Horizontal(g3)
    c: Block(g3)
FEATURE [Part::Extrusion] Extrude047
  Base = -> Sketch049
  Dir = (0,0,1)
  DirMode = 2
  FaceMakerClass = Part::FaceMakerBullseye
  LengthFwd = 6.2
  LengthRev = 0
  Solid = true
  Symmetric = false
FEATURE [Part::Fillet] Fillet054
  Base = -> Extrude047
  Edges = 1 edges r=3.09: [Edge7]
FEATURE [Part::Fillet] Fillet051
  Base = -> Fillet054
  Edges = 1 edges r=3.09: [Edge8]
FEATURE [Part::Fillet] Fillet052
  Base = -> Fillet051
  Edges = 1 edges r=3.09: [Edge17]
FEATURE [Part::Fillet] Fillet053  label="removeFromMainToMakeUSBCableHole001"
  Base = -> Fillet052
  Edges = 1 edges r=3.09: [Edge10]
  Placement = pos=(-111.4,30,14.9) rot=(0,1,0;1.5708rad)
FEATURE [Sketcher::SketchObject] Sketch050
  FullyConstrained = true
  sketch-geometry (4):
    g0: LineSegment StartX=-5.1 StartY=-34.18 StartZ=0 EndX=5.1 EndY=-34.18 EndZ=0
    g1: LineSegment StartX=-5.1 StartY=-3.93167e-07 StartZ=0 EndX=-5.1 EndY=-34.18 EndZ=0
    g2: LineSegment StartX=5.1 StartY=-34.18 StartZ=0 EndX=5.1 EndY=-3.93167e-07 EndZ=0
    g3: LineSegment StartX=-5.1 StartY=-3.93167e-07 StartZ=0 EndX=5.1 EndY=-3.93167e-07 EndZ=0
  constraints (10):
    c: Horizontal(g0)
    c: Block(g0)
    c: Coincident(g1,g0)
    c: Vertical(g1)
    c: Coincident(g2,g0)
    c: Vertical(g2)
    c: Coincident(g3,g1)
    c: Coincident(g3,g2)
    c: Horizontal(g3)
    c: Block(g3)
FEATURE [Part::Extrusion] Extrude048
  Base = -> Sketch050
  Dir = (0,0,1)
  DirMode = 2
  FaceMakerClass = Part::FaceMakerBullseye
  LengthFwd = 6.2
  LengthRev = 0
  Solid = true
  Symmetric = false
FEATURE [Part::Fillet] Fillet058
  Base = -> Extrude048
  Edges = 1 edges r=3.09: [Edge7]
FEATURE [Part::Fillet] Fillet056
  Base = -> Fillet058
  Edges = 1 edges r=3.09: [Edge8]
FEATURE [Part::Fillet] Fillet055
  Base = -> Fillet056
  Edges = 1 edges r=3.09: [Edge17]
FEATURE [Part::Fillet] Fillet057  label="removeFromMainToMakeUSBCableHole002"
  Base = -> Fillet055
  Edges = 1 edges r=3.09: [Edge10]
  Placement = pos=(-111.4,30,18.4) rot=(0,1,0;1.5708rad)
FEATURE [Part::MultiFuse] Fusion050  label="removeFusion050"
  Shapes = -> [Fillet057,Fillet053,Fillet042]
FEATURE [Part::Box] Box082  label="Cube082"
  AttacherType = Attacher::AttachEngine3D
  Height = 3
  Length = 3
  Placement = pos=(-20,-23.5,17) rot=(0,0,1;0rad)
  Width = 23
FEATURE [Part::Box] Box083  label="Cube083"
  AttacherType = Attacher::AttachEngine3D
  Height = 3
  Length = 3
  Placement = pos=(-40,-23.5,17) rot=(0,0,1;0rad)
  Width = 23
FEATURE [Part::Box] Box086  label="Cube086"
  AttacherType = Attacher::AttachEngine3D
  Height = 8
  Length = 28
  Placement = pos=(-132,-26,0) rot=(0,0,1;0rad)
  Width = 23
FEATURE [Part::Box] Box087  label="Cube087"
  AttacherType = Attacher::AttachEngine3D
  Height = 8
  Length = 12
  Placement = pos=(-98,-26,0) rot=(0,0,1;0rad)
  Width = 23
FEATURE [Part::Box] Box088  label="Cube088"
  AttacherType = Attacher::AttachEngine3D
  Height = 8
  Length = 12
  Placement = pos=(-108,-10,0) rot=(0,0,1;0rad)
  Width = 8
FEATURE [Part::MultiFuse] Fusion051  label="extraStrengthFusion051"
  Shapes = -> [Box087,Box088,Box086]
FEATURE [Part::Fillet] Fillet059
  Base = -> Fusion051
  Edges = 1 edges r=4: [Edge8]
FEATURE [Part::MultiFuse] Fusion052  label="main"
  Shapes = -> [Box083,Box082,Cut017,Extrude001,Fillet059,Revolve]
FEATURE [Part::Cut] Cut028
  Base = -> Fusion052
  Tool = -> Fusion050
FEATURE [Part::Fillet] Fillet060
  Base = -> Cut028
  Edges = 1 edges r=2: [Edge287]
FEATURE [Part::Cut] Cut029
  Base = -> Fillet060
  Tool = -> Fillet050
FEATURE [Part::Cut] Cut030
  Base = -> Cut029
  Tool = -> Fusion049
FEATURE [Part::Cut] Cut031  label="mainCut031"
  Base = -> Cut030
  Tool = -> Fusion037
FEATURE [App::MeasureDistance] Distance003  label="Distance: 69.20 mm"
  Distance = 69.2
  P1 = (-2.5,-29.6975,8.49911)
  P2 = (-71.7,-29.6975,8.49911)
FEATURE [App::MeasureDistance] Distance004  label="Distance: 10.00 mm"
  Distance = 10
  P1 = (-56.7,-29.6975,8.49911)
  P2 = (-46.7,-29.6975,8.49911)
FEATURE [Sketcher::SketchObject] Sketch051
  FullyConstrained = true
  MapMode = 4
  Placement = pos=(0,0,0) rot=(0.57735,0.57735,0.57735;2.0944rad)
  sketch-geometry (14):
    g0: LineSegment StartX=6.08745 StartY=-4.11588 StartZ=0 EndX=6.08745 EndY=-2.11589 EndZ=0
    g1: LineSegment StartX=8.08745 StartY=1.38411 StartZ=0 EndX=8.08745 EndY=-1.11589 EndZ=0
    g2: ArcOfCircle CenterX=7.08745 CenterY=-1.11589 CenterZ=0 NormalX=0 NormalY=0 NormalZ=1 AngleXU=0 Radius=1 StartAngle=4.71239 EndAngle=6.28319
    g3: LineSegment StartX=6.08745 StartY=-2.11589 StartZ=0 EndX=7.08745 EndY=-2.11589 EndZ=0
    g4: LineSegment StartX=6.08745 StartY=-4.11588 StartZ=0 EndX=7.08745 EndY=-4.11588 EndZ=0
    g5: ArcOfCircle CenterX=7.08745 CenterY=-1.11589 CenterZ=0 NormalX=0 NormalY=0 NormalZ=1 AngleXU=0 Radius=3 StartAngle=4.71239 EndAngle=6.28319
    g6: ArcOfCircle CenterX=7.08745 CenterY=1.38411 CenterZ=0 NormalX=0 NormalY=0 NormalZ=1 AngleXU=0 Radius=1 StartAngle=5.35e-14 EndAngle=1.5708
    g7: LineSegment StartX=10.0875 StartY=-1.11588 StartZ=0 EndX=10.0875 EndY=1.38411 EndZ=0
    g8: ArcOfCircle CenterX=7.08745 CenterY=1.38411 CenterZ=0 NormalX=0 NormalY=0 NormalZ=1 AngleXU=0 Radius=3 StartAngle=3.57e-14 EndAngle=1.5708
    g9: ArcOfCircle CenterX=4.58745 CenterY=1.38412 CenterZ=0 NormalX=0 NormalY=0 NormalZ=1 AngleXU=0 Radius=1 StartAngle=1.57081 EndAngle=3.14159
    g10: LineSegment StartX=4.58744 StartY=2.38411 StartZ=0 EndX=7.08745 EndY=2.38411 EndZ=0
    g11: LineSegment StartX=4.58745 StartY=4.38411 StartZ=0 EndX=7.08745 EndY=4.38411 EndZ=0
    g12: ArcOfCircle CenterX=4.58745 CenterY=5.38411 CenterZ=0 NormalX=0 NormalY=0 NormalZ=1 AngleXU=0 Radius=1 StartAngle=3.14159 EndAngle=4.71239
    g13: LineSegment StartX=3.58745 StartY=5.38411 StartZ=0 EndX=3.58745 EndY=1.38411 EndZ=0
  constraints (33):
    c: Vertical(g0)
    c: Block(g0)
    c: Block(g1)
    c: Coincident(g2,g1)
    c: Coincident(g3,g0)
    c: Coincident(g3,g2)
    c: Horizontal(g3)
    c: Block(g2)
    c: Coincident(g4,g0)
    c: Horizontal(g4)
    c: Coincident(g5,g2)
    c: Block(g5)
    c: Block(g4)
    c: Coincident(g6,g1)
    c: Block(g6)
    c: Coincident(g7,g5)
    c: Vertical(g7)
    c: Coincident(g8,g6)
    c: Block(g8)
    c: Block(g7)
    c: Coincident(g10,g9)
    c: Coincident(g10,g6)
    c: Horizontal(g10)
    c: Block(g10)
    c: Block(g9)
    c: Coincident(g11,g8)
    c: Horizontal(g11)
    c: Block(g12)
    c: Block(g11)
    c: Coincident(g13,g12)
    c: Coincident(g13,g9)
    c: Vertical(g13)
    c: Tangent(g13,g9)
FEATURE [Part::Extrusion] Extrude049
  Base = -> Sketch051
  Dir = (1,0,0)
  DirMode = 2
  FaceMakerClass = Part::FaceMakerBullseye
  LengthFwd = 10
  LengthRev = 0
  Placement = pos=(-34.55,-22.61,4.115) rot=(0,0,1;3.14159rad)
  Solid = true
  Symmetric = false
